FCSTD DOCUMENT  (FreeCAD 0.19R24291 (Git))
Label: bike light bracket
License: All rights reserved
LicenseURL: http://en.wikipedia.org/wiki/All_rights_reserved
objects: Sketcher::SketchObject×1, PartDesign::Body×1
note: 2 computed .brp shape members not serialized (recipe doc carries the construction recipe); baked Part::Feature solids carry a one-line shape summary decoded from their .brp

FEATURE [Sketcher::SketchObject] Sketch
  FullyConstrained = true
  MapMode = 5
  Support = -> [XY_Plane]
  sketch-geometry (11):
    g0: LineSegment StartX=-46.5 StartY=10 StartZ=0 EndX=46.5 EndY=10 EndZ=0
    g1: LineSegment StartX=46.5 StartY=10 StartZ=0 EndX=46.5 EndY=-10 EndZ=0
    g2: LineSegment StartX=46.5 StartY=-10 StartZ=0 EndX=10 EndY=-10 EndZ=0
    g3: LineSegment StartX=10 StartY=-10 StartZ=0 EndX=10 EndY=-40 EndZ=0
    g4: LineSegment StartX=10 StartY=-40 StartZ=0 EndX=-10 EndY=-40 EndZ=0
    g5: LineSegment StartX=-10 StartY=-40 StartZ=0 EndX=-10 EndY=-10 EndZ=0
    g6: LineSegment StartX=-10 StartY=-10 StartZ=0 EndX=-46.5 EndY=-10 EndZ=0
    g7: LineSegment StartX=-46.5 StartY=-10 StartZ=0 EndX=-46.5 EndY=10 EndZ=0
    g8: Circle CenterX=-36.5 CenterY=0 CenterZ=0 NormalX=0 NormalY=0 NormalZ=1 AngleXU=0 Radius=2.5
    g9: Circle CenterX=36.5 CenterY=0 CenterZ=0 NormalX=0 NormalY=0 NormalZ=1 AngleXU=0 Radius=2.5
    g10: Circle CenterX=0 CenterY=-30 CenterZ=0 NormalX=0 NormalY=0 NormalZ=1 AngleXU=0 Radius=2.5
  constraints (32):
    c: Horizontal(g0)
    c: Coincident(g0,g1)
    c: Coincident(g1,g2)
    c: Horizontal(g2)
    c: Coincident(g2,g3)
    c: Vertical(g3)
    c: Coincident(g3,g4)
    c: Horizontal(g4)
    c: Coincident(g4,g5)
    c: Vertical(g5)
    c: Coincident(g5,g6)
    c: Horizontal(g6)
    c: Coincident(g6,g7)
    c: Coincident(g7,g0)
    c: Vertical(g7)
    c: Vertical(g1)
    c: DistanceX(g0,g0) = 93
    c: Symmetric(g0,g1,g-1)
    c: Equal(g7,g1)
    c: DistanceY(g6,g0) = 20
    c: DistanceY(g5,g5) = 30
    c: Diameter(g8) = 5
    c: PointOnObject(g8,g-1)
    c: DistanceX(g0,g8) = 10
    c: Equal(g6,g2)
    c: DistanceX(g4,g4) = 20
    c: PointOnObject(g9,g-1)
    c: Diameter(g9) = 5
    c: DistanceX(g9,g0) = 10
    c: Diameter(g10) = 5
    c: PointOnObject(g10,g-2)
    c: DistanceY(g3,g10) = 10
FEATURE [PartDesign::Body] Body
  Group = -> [Sketch]
  Origin = -> Origin
